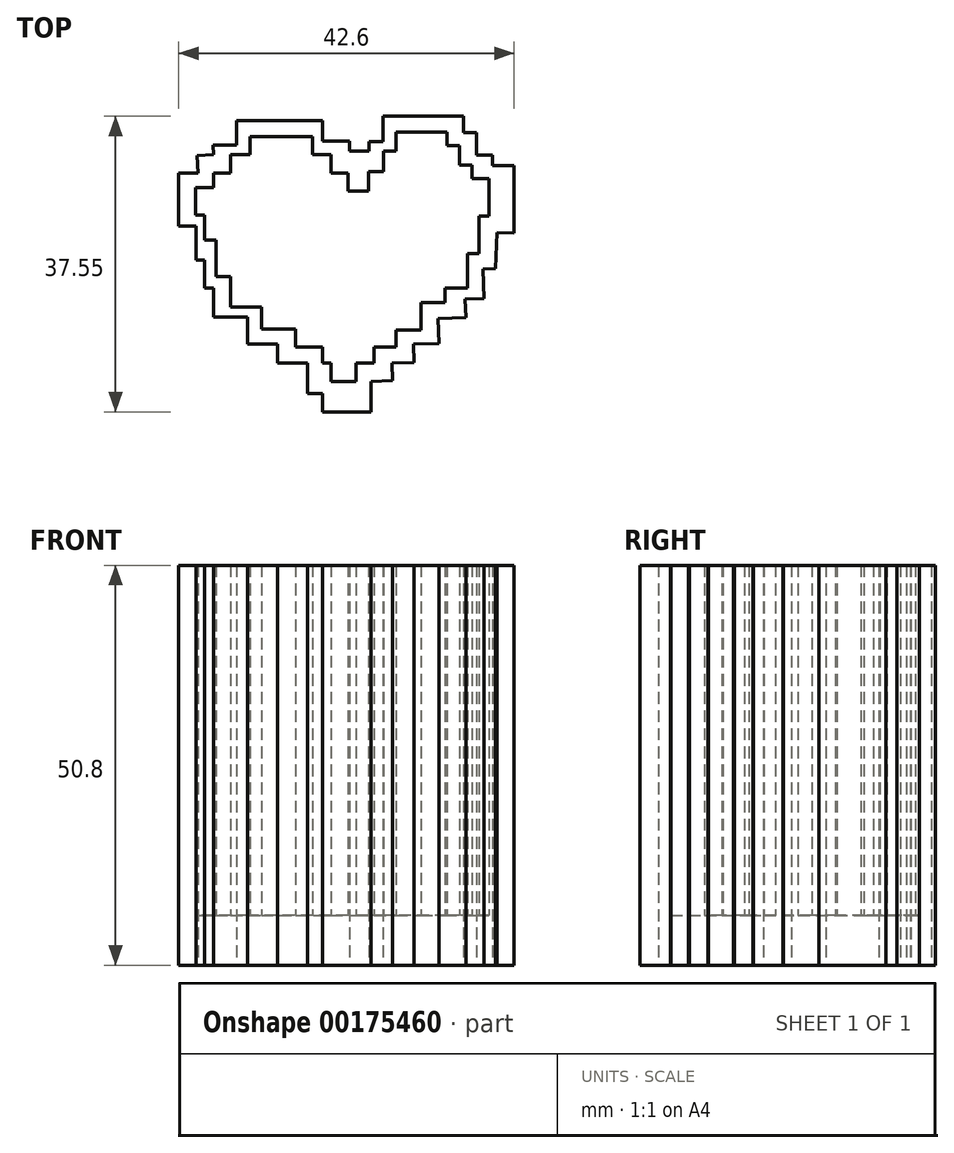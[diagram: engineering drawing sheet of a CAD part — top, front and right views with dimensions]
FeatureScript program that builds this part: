
annotation { "Feature Type Name" : "Feature", "Feature Type Description" : "" }
export const myFeature = defineFeature(function(context is Context, id is Id, definition is map)
    precondition{}
    {
        {
            var Q0;
            Q0=qCreatedBy(makeId("Top.planeOp"),FACE);
            var sketch = newSketch(context, id + "F0", { "sketchPlane" : qUnion([Q0])});
            skLineSegment(sketch, "E0", {"start": v(3.25, 22.29) * mm, "end": v(3.25, 24.17) * mm});
            skLineSegment(sketch, "E1", {"start": v(3.25, 24.17) * mm, "end": v(1.08, 24.17) * mm});
            skLineSegment(sketch, "E2", {"start": v(1.08, 24.17) * mm, "end": v(1.08, 26.48) * mm});
            skLineSegment(sketch, "E3", {"start": v(1.08, 26.48) * mm, "end": v(-1.23, 26.48) * mm});
            skLineSegment(sketch, "E4", {"start": v(-1.23, 26.48) * mm, "end": v(-1.23, 28.8) * mm});
            skLineSegment(sketch, "E5", {"start": v(-1.23, 28.8) * mm, "end": v(-3.4, 28.8) * mm});
            skLineSegment(sketch, "E6", {"start": v(-3.4, 28.8) * mm, "end": v(-6.44, 28.8) * mm});
            skLineSegment(sketch, "E7", {"start": v(-6.44, 28.8) * mm, "end": v(-9.19, 28.8) * mm});
            skLineSegment(sketch, "E8", {"start": v(-9.19, 28.8) * mm, "end": v(-9.19, 26.48) * mm});
            skLineSegment(sketch, "E9", {"start": v(-9.19, 26.48) * mm, "end": v(-11.65, 26.48) * mm});
            skLineSegment(sketch, "E10", {"start": v(-11.65, 26.48) * mm, "end": v(-11.65, 24.17) * mm});
            skLineSegment(sketch, "E11", {"start": v(-11.65, 24.17) * mm, "end": v(-13.82, 24.17) * mm});
            skLineSegment(sketch, "E12", {"start": v(-13.82, 24.17) * mm, "end": v(-13.82, 22.29) * mm});
            skLineSegment(sketch, "E13", {"start": v(-13.82, 22.29) * mm, "end": v(-16.13, 22.29) * mm});
            skLineSegment(sketch, "E14", {"start": v(-16.13, 22.29) * mm, "end": v(-16.13, 18.81) * mm});
            skLineSegment(sketch, "E15", {"start": v(-16.13, 18.81) * mm, "end": v(-14.98, 18.81) * mm});
            skLineSegment(sketch, "E16", {"start": v(-14.98, 18.81) * mm, "end": v(-14.98, 15.63) * mm});
            skLineSegment(sketch, "E17", {"start": v(-14.98, 15.63) * mm, "end": v(-13.53, 15.63) * mm});
            skLineSegment(sketch, "E18", {"start": v(-13.53, 15.63) * mm, "end": v(-13.53, 11) * mm});
            skLineSegment(sketch, "E19", {"start": v(-13.53, 11) * mm, "end": v(-11.65, 11) * mm});
            skLineSegment(sketch, "E20", {"start": v(-11.65, 11) * mm, "end": v(-11.65, 7.1) * mm});
            skLineSegment(sketch, "E21", {"start": v(-11.65, 7.1) * mm, "end": v(-7.74, 7.1) * mm});
            skLineSegment(sketch, "E22", {"start": v(-7.74, 7.1) * mm, "end": v(-7.74, 4.35) * mm});
            skLineSegment(sketch, "E23", {"start": v(-7.74, 4.35) * mm, "end": v(-3.4, 4.35) * mm});
            skLineSegment(sketch, "E24", {"start": v(-3.4, 4.35) * mm, "end": v(-3.4, 2.03) * mm});
            skLineSegment(sketch, "E25", {"start": v(-3.4, 2.03) * mm, "end": v(0, 2.03) * mm});
            skLineSegment(sketch, "E26", {"start": v(0, 2.03) * mm, "end": v(0, 0) * mm});
            skLineSegment(sketch, "E27", {"start": v(0, 0) * mm, "end": v(1.08, 0) * mm});
            skLineSegment(sketch, "E28", {"start": v(1.08, 0) * mm, "end": v(1.08, -2.3) * mm});
            skLineSegment(sketch, "E29", {"start": v(1.08, -2.3) * mm, "end": v(4.27, -2.3) * mm});
            skLineSegment(sketch, "E30", {"start": v(4.27, -2.3) * mm, "end": v(4.27, 0) * mm});
            skLineSegment(sketch, "E31", {"start": v(4.27, 0) * mm, "end": v(6.58, 0) * mm});
            skLineSegment(sketch, "E32", {"start": v(6.58, 0) * mm, "end": v(6.58, 2.03) * mm});
            skPoint(sketch, "E32.endSnap0", {"position": v(-1.7, 2.03) * mm});
            skLineSegment(sketch, "E33", {"start": v(6.58, 2.03) * mm, "end": v(9.33, 2.03) * mm});
            skLineSegment(sketch, "E34", {"start": v(9.33, 2.03) * mm, "end": v(9.33, 4.2) * mm});
            skLineSegment(sketch, "E35", {"start": v(9.33, 4.2) * mm, "end": v(12.51, 4.2) * mm});
            skLineSegment(sketch, "E36", {"start": v(12.51, 4.2) * mm, "end": v(12.51, 7.67) * mm});
            skLineSegment(sketch, "E37", {"start": v(12.51, 7.67) * mm, "end": v(15.55, 7.67) * mm});
            skLineSegment(sketch, "E38", {"start": v(15.55, 7.67) * mm, "end": v(15.55, 9.55) * mm});
            skLineSegment(sketch, "E39", {"start": v(15.55, 9.55) * mm, "end": v(18.44, 9.55) * mm});
            skLineSegment(sketch, "E40", {"start": v(18.44, 9.55) * mm, "end": v(18.44, 13.9) * mm});
            skLineSegment(sketch, "E41", {"start": v(18.44, 13.9) * mm, "end": v(19.9, 13.9) * mm});
            skLineSegment(sketch, "E42", {"start": v(19.9, 13.9) * mm, "end": v(19.9, 18.67) * mm});
            skLineSegment(sketch, "E43", {"start": v(19.9, 18.67) * mm, "end": v(21.2, 18.67) * mm});
            skLineSegment(sketch, "E44", {"start": v(21.2, 18.67) * mm, "end": v(21.2, 23.44) * mm});
            skLineSegment(sketch, "E45", {"start": v(21.2, 23.44) * mm, "end": v(19.02, 23.44) * mm});
            skLineSegment(sketch, "E46", {"start": v(19.02, 23.44) * mm, "end": v(19.02, 25.18) * mm});
            skLineSegment(sketch, "E47", {"start": v(19.02, 25.18) * mm, "end": v(17.43, 25.18) * mm});
            skLineSegment(sketch, "E48", {"start": v(17.43, 25.18) * mm, "end": v(17.43, 27.64) * mm});
            skLineSegment(sketch, "E49", {"start": v(17.43, 27.64) * mm, "end": v(15.84, 27.64) * mm});
            skLineSegment(sketch, "E50", {"start": v(15.84, 27.64) * mm, "end": v(15.84, 29.37) * mm});
            skLineSegment(sketch, "E51", {"start": v(15.84, 29.37) * mm, "end": v(9.33, 29.37) * mm});
            skLineSegment(sketch, "E52", {"start": v(9.33, 29.37) * mm, "end": v(9.33, 26.91) * mm});
            skLineSegment(sketch, "E53", {"start": v(9.33, 26.91) * mm, "end": v(7.74, 26.91) * mm});
            skLineSegment(sketch, "E54", {"start": v(7.74, 26.91) * mm, "end": v(7.74, 24.31) * mm});
            skLineSegment(sketch, "E55", {"start": v(7.74, 24.31) * mm, "end": v(5.86, 24.31) * mm});
            skLineSegment(sketch, "E56", {"start": v(5.86, 24.31) * mm, "end": v(5.86, 21.85) * mm});
            skLineSegment(sketch, "E57", {"start": v(5.86, 21.85) * mm, "end": v(3.25, 21.85) * mm});
            skLineSegment(sketch, "E58", {"start": v(3.25, 21.85) * mm, "end": v(3.25, 24.17) * mm});
            skPoint(sketch, "E59.startSnap0", {"position": v(4.55, 21.85) * mm});
            skLineSegment(sketch, "E60", {"start": v(0, 30.82) * mm, "end": v(-10.88, 30.82) * mm});
            skLineSegment(sketch, "E61", {"start": v(-10.88, 30.82) * mm, "end": v(-10.88, 27.68) * mm});
            skLineSegment(sketch, "E62", {"start": v(-10.88, 27.68) * mm, "end": v(-13.89, 27.68) * mm});
            skLineSegment(sketch, "E63", {"start": v(-13.89, 27.68) * mm, "end": v(-13.82, 26.48) * mm});
            skLineSegment(sketch, "E64", {"start": v(-13.82, 26.48) * mm, "end": v(-15.93, 26.36) * mm});
            skLineSegment(sketch, "E65", {"start": v(-15.93, 26.36) * mm, "end": v(-15.8, 24.17) * mm});
            skLineSegment(sketch, "E66", {"start": v(-15.8, 24.17) * mm, "end": v(-18.26, 24.17) * mm});
            skLineSegment(sketch, "E67", {"start": v(-18.26, 24.17) * mm, "end": v(-18.26, 17.44) * mm});
            skLineSegment(sketch, "E68", {"start": v(-18.26, 17.44) * mm, "end": v(-16.07, 17.44) * mm});
            skLineSegment(sketch, "E69", {"start": v(-16.07, 17.44) * mm, "end": v(-16.07, 13.07) * mm});
            skLineSegment(sketch, "E70", {"start": v(-16.07, 13.07) * mm, "end": v(-14.98, 13.07) * mm});
            skLineSegment(sketch, "E71", {"start": v(-14.98, 13.07) * mm, "end": v(-14.98, 9.52) * mm});
            skLineSegment(sketch, "E72", {"start": v(-14.98, 9.52) * mm, "end": v(-13.82, 9.52) * mm});
            skLineSegment(sketch, "E73", {"start": v(-13.82, 9.52) * mm, "end": v(-13.82, 5.83) * mm});
            skLineSegment(sketch, "E74", {"start": v(-13.82, 5.83) * mm, "end": v(-9.52, 5.83) * mm});
            skLineSegment(sketch, "E75", {"start": v(-9.52, 5.83) * mm, "end": v(-9.52, 2.41) * mm});
            skLineSegment(sketch, "E76", {"start": v(-9.52, 2.41) * mm, "end": v(-5.7, 2.41) * mm});
            skLineSegment(sketch, "E77", {"start": v(-5.7, 2.41) * mm, "end": v(-5.7, 0) * mm});
            skLineSegment(sketch, "E78", {"start": v(-5.7, 0) * mm, "end": v(-1.87, 0) * mm});
            skLineSegment(sketch, "E79", {"start": v(-1.87, 0) * mm, "end": v(-1.87, -3.87) * mm});
            skLineSegment(sketch, "E80", {"start": v(-1.87, -3.87) * mm, "end": v(0, -3.87) * mm});
            skLineSegment(sketch, "E81", {"start": v(0, -3.87) * mm, "end": v(0, -6.19) * mm});
            skLineSegment(sketch, "E82", {"start": v(0, -6.19) * mm, "end": v(6.19, -6.19) * mm});
            skLineSegment(sketch, "E83", {"start": v(6.19, -6.19) * mm, "end": v(6.19, -2.3) * mm});
            skLineSegment(sketch, "E84", {"start": v(6.19, -2.3) * mm, "end": v(8.92, -2.23) * mm});
            skLineSegment(sketch, "E85", {"start": v(8.92, -2.23) * mm, "end": v(8.85, 0) * mm});
            skLineSegment(sketch, "E86", {"start": v(8.85, 0) * mm, "end": v(11.64, 0.08) * mm});
            skLineSegment(sketch, "E87", {"start": v(11.64, 0.08) * mm, "end": v(11.57, 2.41) * mm});
            skLineSegment(sketch, "E88", {"start": v(11.57, 2.41) * mm, "end": v(14.78, 2.51) * mm});
            skLineSegment(sketch, "E89", {"start": v(14.78, 2.51) * mm, "end": v(14.69, 5.69) * mm});
            skLineSegment(sketch, "E90", {"start": v(14.69, 5.69) * mm, "end": v(18.21, 5.8) * mm});
            skLineSegment(sketch, "E91", {"start": v(18.21, 5.8) * mm, "end": v(18.14, 8.14) * mm});
            skLineSegment(sketch, "E92", {"start": v(18.14, 8.14) * mm, "end": v(20.53, 8.2) * mm});
            skLineSegment(sketch, "E93", {"start": v(20.53, 8.2) * mm, "end": v(20.39, 11.97) * mm});
            skLineSegment(sketch, "E94", {"start": v(20.39, 11.97) * mm, "end": v(22.02, 12.03) * mm});
            skLineSegment(sketch, "E95", {"start": v(22.02, 12.03) * mm, "end": v(22.16, 16.62) * mm});
            skLineSegment(sketch, "E96", {"start": v(22.16, 16.62) * mm, "end": v(24.34, 16.55) * mm});
            skLineSegment(sketch, "E97", {"start": v(24.34, 16.55) * mm, "end": v(24.34, 25.08) * mm});
            skLineSegment(sketch, "E98", {"start": v(24.34, 25.08) * mm, "end": v(21.62, 25.08) * mm});
            skLineSegment(sketch, "E99", {"start": v(21.62, 25.08) * mm, "end": v(21.62, 26.45) * mm});
            skLineSegment(sketch, "E100", {"start": v(21.62, 26.45) * mm, "end": v(19.57, 26.45) * mm});
            skLineSegment(sketch, "E101", {"start": v(19.57, 26.45) * mm, "end": v(19.57, 29.32) * mm});
            skLineSegment(sketch, "E102", {"start": v(19.57, 29.32) * mm, "end": v(17.93, 29.32) * mm});
            skLineSegment(sketch, "E103", {"start": v(17.93, 29.32) * mm, "end": v(17.93, 31.36) * mm});
            skLineSegment(sketch, "E104", {"start": v(17.93, 31.36) * mm, "end": v(7.69, 31.36) * mm});
            skLineSegment(sketch, "E105", {"start": v(7.69, 31.36) * mm, "end": v(7.69, 28.14) * mm});
            skPoint(sketch, "E105.endSnap0", {"position": v(9.33, 28.14) * mm});
            skLineSegment(sketch, "E106", {"start": v(7.69, 28.14) * mm, "end": v(5.91, 28.14) * mm});
            skPoint(sketch, "E59.start.orphan", {"position": v(4.55, 25.18) * mm});
            skLineSegment(sketch, "E107", {"start": v(5.91, 28.14) * mm, "end": v(5.91, 26.91) * mm});
            skPoint(sketch, "E108.start.orphan", {"position": v(0, 27.68) * mm});
            skLineSegment(sketch, "E109", {"start": v(5.91, 26.91) * mm, "end": v(3.46, 26.91) * mm});
            skLineSegment(sketch, "E110", {"start": v(3.46, 26.91) * mm, "end": v(3.46, 28.22) * mm});
            skLineSegment(sketch, "E111", {"start": v(3.46, 28.22) * mm, "end": v(0, 28.22) * mm});
            skLineSegment(sketch, "E112", {"start": v(0, 30.82) * mm, "end": v(0, 28.22) * mm});
            skSolve(sketch);
        }
        {
            var Q0;
            {var subQ1=sQuery(id+"F0.wireOp",EDGE,"E1");Q0=makeQuery(id+"F0.imprint","IMPRINT",FACE,{"disambiguationData":[TD([[makeQuery(id+"F0.imprint","IMPRINT",EDGE,{"derivedFrom":subQ1}),1.0]])]});}
            extrude(context, id + "F1", {"entities" : qUnion([Q0]), "depth" : 6.35 * mm});
        }
        {
            var Q0;
            {var subQ1=sQuery(id+"F0.wireOp",EDGE,"E1");Q0=makeQuery(id+"F0.imprint","IMPRINT",FACE,{"disambiguationData":[TD([[makeQuery(id+"F0.imprint","IMPRINT",EDGE,{"derivedFrom":subQ1}),-1.0]])]});}
            extrude(context, id + "F2", {"entities" : qUnion([Q0]), "operationType" : NewBodyOperationType.ADD, "depth" : 50.8 * mm});
        }
    });
